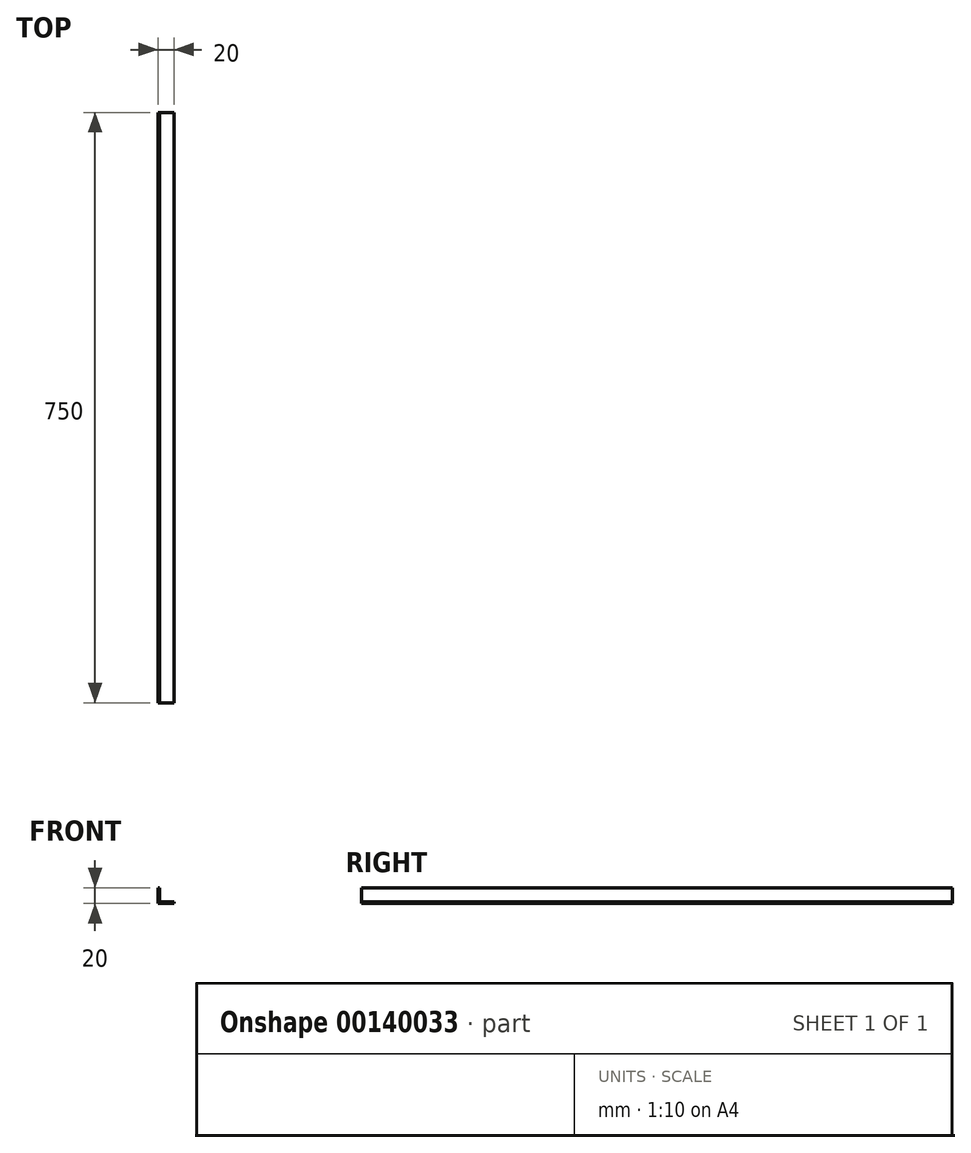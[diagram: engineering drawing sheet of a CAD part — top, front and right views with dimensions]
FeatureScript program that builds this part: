
annotation { "Feature Type Name" : "Feature", "Feature Type Description" : "" }
export const myFeature = defineFeature(function(context is Context, id is Id, definition is map)
    precondition{}
    {
        {
            var Q0;
            Q0=qCreatedBy(makeId("Front.planeOp"),FACE);
            var sketch = newSketch(context, id + "F0", { "sketchPlane" : qUnion([Q0])});
            skLineSegment(sketch, "E0", {"start": v(0, 0) * mm, "end": v(20, 0) * mm});
            skLineSegment(sketch, "E1", {"start": v(20, 0) * mm, "end": v(20, 2) * mm});
            skLineSegment(sketch, "E2", {"start": v(20, 2) * mm, "end": v(2, 2) * mm});
            skLineSegment(sketch, "E3", {"start": v(2, 2) * mm, "end": v(2, 20) * mm});
            skLineSegment(sketch, "E4", {"start": v(2, 20) * mm, "end": v(0, 20) * mm});
            skLineSegment(sketch, "E5", {"start": v(0, 20) * mm, "end": v(0, 0) * mm});
            skSolve(sketch);
        }
        {
            var Q0;
            Q0=qSketchRegion(id+"F0",true);
            extrude(context, id + "F1", {"entities" : qUnion([Q0]), "endBound" : BoundingType.SYMMETRIC, "depth" : 750 * mm});
        }
    });
